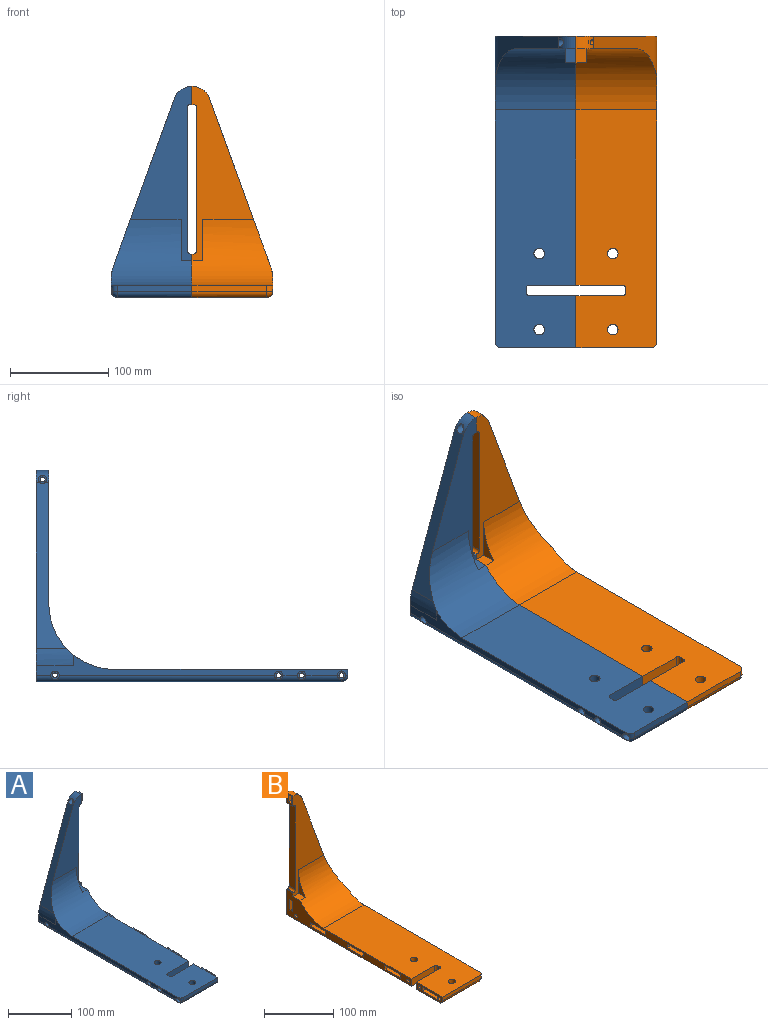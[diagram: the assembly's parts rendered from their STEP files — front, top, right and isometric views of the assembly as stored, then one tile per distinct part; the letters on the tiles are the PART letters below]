
ASSEMBLY  parts=2 mates=1
PART A: 103 faces, bbox 89.6x318.3x216.2 mm
  f0: plane 3.81x1.78mm, normal (1,0,0), area 5.5mm2, adj f79,f80,f81,f82
  f1: cylinder r=19.05mm len=17.9mm, axis (0,1,0), area 230.7mm2, adj f8,f12,f20,f26,f76
  f2: plane 311.15x20.61mm, normal (-1,0,0), area 2200.3mm2, adj f9,f10,f21,f22,f26,f27,f34,f68
  f3: cylinder r=2.54mm len=69.8mm, axis (1,0,0), area 1114mm2, adj f36,f75
  f4: cylinder r=2.54mm len=69.8mm, axis (1,0,0), area 1114mm2, adj f36,f73
  f5: cylinder r=2.54mm len=69.8mm, axis (1,0,0), area 1114mm2, adj f7,f71
  f6: cylinder r=2.54mm len=69.8mm, axis (1,0,0), area 1114mm2, adj f7,f69
  f7: plane 253.49x44.45mm, normal (1,0,0), area 3618.5mm2, adj f5,f6,f9,f10,f11,f12,f14,f18
  f8: plane 18.57x12.7mm, normal (1,0,0), area 155.2mm2, adj f1,f12,f13,f26,f37,f38,f39,f40
  f9: cylinder r=66.9mm len=82.5mm, axis (-1,0,0), area 7217.9mm2, adj f2,f7,f10,f12,f19,f20,f21,f34
  f10: plane 242.57x82.5mm, normal (0,0,1), area 19276.3mm2, adj f2,f7,f9,f15,f17,f18,f27,f29
  f11: plane 311.15x76.15mm, normal (0,0,-1), area 22967mm2, adj f7,f16,f17,f18,f22,f26,f29,f30
  f12: plane 177.32x62.83mm, normal (0,-1,0), area 4884.6mm2, adj f1,f7,f8,f9,f13,f14,f19,f20
  f13: plane 12.7x1.59mm, normal (0,0,-1), area 20.2mm2, adj f8,f12,f25,f26
  f14: plane 12.7x1.59mm, normal (0,0,1), area 20.2mm2, adj f7,f12,f23,f26
  f15: plane 76.15x6.35mm, normal (0,-1,0), area 483.6mm2, adj f10,f16,f27,f36
  f16: cylinder r=6.35mm len=76.15mm, axis (-1,0,0), area 759.6mm2, adj f11,f15,f28,f36
  f17: plane 47.63x12.7mm, normal (0,1,0), area 604.8mm2, adj f10,f11,f30,f36
  f18: plane 47.63x12.7mm, normal (0,-1,0), area 604.8mm2, adj f7,f10,f11,f31
  f19: plane 14.3x11.11mm, normal (0,0,1), area 158.9mm2, adj f7,f9,f12,f35
  f20: plane 169.83x62.3mm, normal (-0.94,0,0.34), area 2553.6mm2, adj f1,f9,f12,f21,f26,f76
  f21: cylinder r=50.8mm len=38.1mm, axis (0,1,0), area 649.1mm2, adj f2,f9,f20,f26,f34
  f22: cylinder r=6.35mm len=311.15mm, axis (0,1,0), area 2999.9mm2, adj f2,f11,f26,f28,f68,f70,f72,f74
  f23: cylinder r=3.18mm len=12.7mm, axis (0,1,0), area 63.3mm2, adj f12,f14,f24,f26
  f24: plane 146.05x12.7mm, normal (1,0,0), area 1854.8mm2, adj f12,f23,f25,f26
  f25: cylinder r=3.17mm len=12.7mm, axis (0,1,0), area 63.3mm2, adj f12,f13,f24,f26
  f26: plane 215.42x82.5mm, normal (0,1,0), area 10433.9mm2, adj f1,f2,f7,f8,f11,f13,f14,f20
  f27: cylinder r=6.35mm len=6.35mm, axis (0,0,1), area 47.8mm2, adj f2,f10,f15,f28,f72
  f28: bspline ~9.47x6.35mm, area 46.7mm2, adj f16,f22,f27,f72
  f29: plane 12.7x4.45mm, normal (1,0,0), area 56.5mm2, adj f10,f11,f30,f31
  f30: cylinder r=3.17mm len=12.7mm, axis (0,0,1), area 63.3mm2, adj f10,f11,f17,f29
  f31: cylinder r=3.17mm len=12.7mm, axis (0,0,1), area 63.3mm2, adj f10,f11,f18,f29
  f32: cylinder r=5.4mm len=12.7mm, axis (0,0,1), area 430.7mm2, adj f10,f11
  f33: cylinder r=5.4mm len=12.7mm, axis (0,0,1), area 430.7mm2, adj f10,f11
  f34: plane 10.52x1.1mm, normal (0,1,0), area 3.8mm2, adj f2,f9,f21
  f35: plane 41.33x14.3mm, normal (1,0,0), area 187.7mm2, adj f9,f12,f19
  f36: plane 53.21x12.7mm, normal (1,0,0), area 425mm2, adj f3,f4,f10,f11,f15,f16,f17,f48
  f37: plane 12.7x5.08mm, normal (0,1,0), area 64.5mm2, adj f8,f38,f40,f80
  f38: plane 6.35x5.08mm, normal (0,0,1), area 32.3mm2, adj f8,f37,f39,f78
  f39: plane 12.7x5.08mm, normal (0,-1,0), area 64.5mm2, adj f8,f38,f40,f81
  f40: plane 6.35x5.08mm, normal (0,0,-1), area 32.3mm2, adj f8,f37,f39,f82
  f41: cylinder r=2.54mm len=14.48mm, axis (-1,0,0), area 231.1mm2, adj f77,f79
  f42: plane 3.81x1.78mm, normal (1,0,0), area 5.5mm2, adj f78,f79,f80,f81
  f43: plane 6.35x5.08mm, normal (0,0,1), area 32.3mm2, adj f7,f44,f46,f84
  f44: plane 19.05x5.08mm, normal (0,-1,0), area 96.8mm2, adj f7,f43,f45,f86
  f45: plane 6.35x5.08mm, normal (0,0,-1), area 32.3mm2, adj f7,f44,f46,f85
  f46: plane 19.05x5.08mm, normal (0,1,0), area 96.8mm2, adj f7,f43,f45,f83
  f47: plane 16.51x3.81mm, normal (1,0,0), area 62.9mm2, adj f83,f84,f85,f86
  f48: plane 31.75x5.08mm, normal (0,0,1), area 161.3mm2, adj f36,f49,f51,f99
  f49: plane 6.35x5.08mm, normal (0,-1,0), area 32.3mm2, adj f36,f48,f50,f100
  f50: plane 31.75x5.08mm, normal (0,0,-1), area 161.3mm2, adj f36,f49,f51,f102
  f51: plane 6.35x5.08mm, normal (0,1,0), area 32.3mm2, adj f36,f48,f50,f101
  f52: plane 29.21x3.81mm, normal (1,0,0), area 111.3mm2, adj f99,f100,f101,f102
  f53: plane 6.35x5.08mm, normal (0,-1,0), area 32.3mm2, adj f7,f54,f56,f96
  f54: plane 31.75x5.08mm, normal (0,0,-1), area 161.3mm2, adj f7,f53,f55,f98
  f55: plane 6.35x5.08mm, normal (0,1,0), area 32.3mm2, adj f7,f54,f56,f97
  f56: plane 31.75x5.08mm, normal (0,0,1), area 161.3mm2, adj f7,f53,f55,f95
  f57: plane 29.21x3.81mm, normal (1,0,0), area 111.3mm2, adj f95,f96,f97,f98
  f58: plane 6.35x5.08mm, normal (0,-1,0), area 32.3mm2, adj f7,f59,f61,f91
  f59: plane 31.75x5.08mm, normal (0,0,-1), area 161.3mm2, adj f7,f58,f60,f93
  f60: plane 6.35x5.08mm, normal (0,1,0), area 32.3mm2, adj f7,f59,f61,f94
  f61: plane 31.75x5.08mm, normal (0,0,1), area 161.3mm2, adj f7,f58,f60,f92
  f62: plane 29.21x3.81mm, normal (1,0,0), area 111.3mm2, adj f91,f92,f93,f94
  f63: plane 6.35x5.08mm, normal (0,-1,0), area 32.3mm2, adj f7,f64,f66,f88
  f64: plane 31.75x5.08mm, normal (0,0,-1), area 161.3mm2, adj f7,f63,f65,f90
  f65: plane 6.35x5.08mm, normal (0,1,0), area 32.3mm2, adj f7,f64,f66,f89
  f66: plane 31.75x5.08mm, normal (0,0,1), area 161.3mm2, adj f7,f63,f65,f87
  f67: plane 29.21x3.81mm, normal (1,0,0), area 111.3mm2, adj f87,f88,f89,f90
  f68: cylinder r=4.31mm len=12.7mm, axis (-1,0,0), area 343.5mm2, adj f2,f22,f69
  f69: plane 8.61x8.61mm, normal (-1,0,0), area 38mm2, adj f6,f68
  f70: cylinder r=4.31mm len=12.7mm, axis (-1,0,0), area 343.5mm2, adj f2,f22,f71
  f71: plane 8.61x8.61mm, normal (-1,0,0), area 38mm2, adj f5,f70
  f72: cylinder r=4.31mm len=12.7mm, axis (-1,0,0), area 320.8mm2, adj f2,f22,f27,f28,f73
  f73: plane 8.61x8.61mm, normal (-1,0,0), area 38mm2, adj f4,f72
  f74: cylinder r=4.31mm len=12.7mm, axis (-1,0,0), area 343.5mm2, adj f2,f22,f75
  f75: plane 8.61x8.61mm, normal (-1,0,0), area 38mm2, adj f3,f74
  f76: cylinder r=4.31mm len=8.61mm, axis (-1,0,0), area 176mm2, adj f1,f20,f77
  f77: plane 8.61x8.61mm, normal (-1,0,0), area 38mm2, adj f41,f76
  f78: cylinder r=1.27mm len=6.35mm, axis (0,1,0), area 10.1mm2, adj f38,f42,f80,f81
  f79: torus R=3.81mm, axis (1,0,0), area 27.4mm2, adj f0,f41,f42,f80,f81
  f80: cylinder r=1.27mm len=12.7mm, axis (0,0,-1), area 18.3mm2, adj f0,f37,f42,f78,f79,f82
  f81: cylinder r=1.27mm len=12.7mm, axis (0,0,1), area 18.3mm2, adj f0,f39,f42,f78,f79,f82
  f82: cylinder r=1.27mm len=6.35mm, axis (0,-1,0), area 10.1mm2, adj f0,f40,f80,f81
  f83: cylinder r=1.27mm len=19.05mm, axis (0,0,-1), area 35.5mm2, adj f46,f47,f84,f85
  f84: cylinder r=1.27mm len=6.35mm, axis (0,1,0), area 10.1mm2, adj f43,f47,f83,f86
  f85: cylinder r=1.27mm len=6.35mm, axis (0,-1,0), area 10.1mm2, adj f45,f47,f83,f86
  f86: cylinder r=1.27mm len=19.05mm, axis (0,0,1), area 35.5mm2, adj f44,f47,f84,f85
  f87: cylinder r=1.27mm len=31.75mm, axis (0,1,0), area 60.8mm2, adj f66,f67,f88,f89
  f88: cylinder r=1.27mm len=6.35mm, axis (0,0,1), area 10.1mm2, adj f63,f67,f87,f90
  f89: cylinder r=1.27mm len=6.35mm, axis (0,0,-1), area 10.1mm2, adj f65,f67,f87,f90
  f90: cylinder r=1.27mm len=31.75mm, axis (0,-1,0), area 60.8mm2, adj f64,f67,f88,f89
  f91: cylinder r=1.27mm len=6.35mm, axis (0,0,1), area 10.1mm2, adj f58,f62,f92,f93
  f92: cylinder r=1.27mm len=31.75mm, axis (0,1,0), area 60.8mm2, adj f61,f62,f91,f94
  f93: cylinder r=1.27mm len=31.75mm, axis (0,-1,0), area 60.8mm2, adj f59,f62,f91,f94
  f94: cylinder r=1.27mm len=6.35mm, axis (0,0,-1), area 10.1mm2, adj f60,f62,f92,f93
  f95: cylinder r=1.27mm len=31.75mm, axis (0,1,0), area 60.8mm2, adj f56,f57,f96,f97
  f96: cylinder r=1.27mm len=6.35mm, axis (0,0,1), area 10.1mm2, adj f53,f57,f95,f98
  f97: cylinder r=1.27mm len=6.35mm, axis (0,0,-1), area 10.1mm2, adj f55,f57,f95,f98
  f98: cylinder r=1.27mm len=31.75mm, axis (0,-1,0), area 60.8mm2, adj f54,f57,f96,f97
  f99: cylinder r=1.27mm len=31.75mm, axis (0,1,0), area 60.8mm2, adj f48,f52,f100,f101
  f100: cylinder r=1.27mm len=6.35mm, axis (0,0,1), area 10.1mm2, adj f49,f52,f99,f102
  f101: cylinder r=1.27mm len=6.35mm, axis (0,0,-1), area 10.1mm2, adj f51,f52,f99,f102
  f102: cylinder r=1.27mm len=31.75mm, axis (0,-1,0), area 60.8mm2, adj f50,f52,f100,f101
PART B: 116 faces, bbox 82.6x317.5x215.4 mm
  f0: cylinder r=2.54mm len=5.08mm, axis (-1,0,0), area 56.2mm2, adj f8,f110
  f1: cylinder r=2.54mm len=62.23mm, axis (-1,0,0), area 993.1mm2, adj f6,f107
  f2: cylinder r=2.54mm len=62.23mm, axis (-1,0,0), area 993.1mm2, adj f6,f99
  f3: cylinder r=2.54mm len=62.23mm, axis (-1,0,0), area 993.1mm2, adj f5,f91
  f4: cylinder r=2.54mm len=62.23mm, axis (-1,0,0), area 993.1mm2, adj f5,f83
  f5: plane 253.49x44.45mm, normal (-1,0,0), area 3653.7mm2, adj f3,f4,f12,f14,f15,f16,f23,f25
  f6: plane 53.21x12.7mm, normal (-1,0,0), area 434.6mm2, adj f1,f2,f14,f15,f26,f27,f28,f51
  f7: plane 18.57x12.7mm, normal (-1,0,0), area 159.9mm2, adj f8,f16,f19,f25,f46,f47,f48,f49
  f8: cylinder r=19.05mm len=17.9mm, axis (0,1,0), area 271.7mm2, adj f0,f7,f16,f17,f25,f108,f109,f110
  f9: cylinder r=6.35mm len=311.15mm, axis (0,1,0), area 3069.2mm2, adj f10,f15,f18,f25,f42,f43,f44,f45
  f10: bspline ~9.47x6.35mm, area 59.7mm2, adj f9,f11,f27,f43
  f11: cylinder r=6.35mm len=6.35mm, axis (0,0,-1), area 60mm2, adj f10,f14,f18,f26,f43
  f12: cylinder r=66.9mm len=82.6mm, axis (-1,0,0), area 7223.1mm2, adj f5,f13,f14,f16,f17,f24,f36,f37
  f13: plane 36.83x14.26mm, normal (1,0,0), area 183.8mm2, adj f12,f36,f37
  f14: plane 242.57x82.5mm, normal (0,0,1), area 19276.3mm2, adj f5,f6,f11,f12,f18,f26,f28,f29
  f15: plane 311.15x76.15mm, normal (0,0,-1), area 22967mm2, adj f5,f6,f9,f25,f27,f28,f29,f30
  f16: plane 177.32x62.83mm, normal (0,-1,0), area 4884.6mm2, adj f5,f7,f8,f12,f17,f19,f20,f21
  f17: plane 169.07x61.54mm, normal (0.94,0,0.34), area 2558mm2, adj f8,f12,f16,f24,f25
  f18: plane 311.15x10.09mm, normal (1,0,0), area 1987.9mm2, adj f9,f11,f14,f24,f25,f35,f36,f42
  f19: plane 12.7x1.59mm, normal (0,0,-1), area 20.2mm2, adj f7,f16,f20,f25
  f20: cylinder r=3.18mm len=12.7mm, axis (0,1,0), area 63.3mm2, adj f16,f19,f21,f25
  f21: plane 146.05x12.7mm, normal (-1,0,0), area 1854.8mm2, adj f16,f20,f22,f25
  f22: cylinder r=3.17mm len=12.7mm, axis (0,1,0), area 63.3mm2, adj f16,f21,f23,f25
  f23: plane 12.7x1.59mm, normal (0,0,1), area 20.2mm2, adj f5,f16,f22,f25
  f24: cylinder r=50.8mm len=38.1mm, axis (0,1,0), area 649.1mm2, adj f12,f17,f18,f25,f37,f38
  f25: plane 215.42x82.5mm, normal (0,1,0), area 10433.9mm2, adj f5,f7,f8,f9,f15,f17,f18,f19
  f26: plane 76.15x6.35mm, normal (0,-1,0), area 483.6mm2, adj f6,f11,f14,f27
  f27: cylinder r=6.35mm len=76.15mm, axis (-1,0,0), area 759.6mm2, adj f6,f10,f15,f26
  f28: plane 47.63x12.7mm, normal (0,1,0), area 604.8mm2, adj f6,f14,f15,f29
  f29: cylinder r=3.17mm len=12.7mm, axis (0,0,1), area 63.3mm2, adj f14,f15,f28,f30
  f30: plane 12.7x4.45mm, normal (-1,0,0), area 56.5mm2, adj f14,f15,f29,f31
  f31: cylinder r=3.17mm len=12.7mm, axis (0,0,1), area 63.3mm2, adj f14,f15,f30,f32
  f32: plane 47.63x12.7mm, normal (0,-1,0), area 604.8mm2, adj f5,f14,f15,f31
  f33: cylinder r=5.4mm len=12.7mm, axis (0,0,1), area 430.7mm2, adj f14,f15
  f34: cylinder r=5.4mm len=12.7mm, axis (0,0,1), area 430.7mm2, adj f14,f15
  f35: plane 3.74x0.1mm, normal (0,1,0), area 0.2mm2, adj f18,f36,f38
  f36: plane 62.23x0.1mm, normal (0,0,-1), area 6.2mm2, adj f12,f13,f18,f35,f38
  f37: plane 14.26x1.2mm, normal (0,1,0), area 5.1mm2, adj f12,f13,f24,f38
  f38: plane 25.4x3.74mm, normal (1,0,0.03), area 95.1mm2, adj f24,f35,f36,f37
  f39: plane 14.3x11.11mm, normal (0,0,1), area 158.9mm2, adj f5,f12,f16,f40
  f40: plane 41.33x14.3mm, normal (-1,0,0), area 187.7mm2, adj f12,f16,f39
  f41: cylinder r=2.54mm len=5.08mm, axis (-1,0,0), area 25.9mm2, adj f50,f115
  f42: cylinder r=2.54mm len=16.16mm, axis (-1,0,0), area 257.8mm2, adj f9,f18,f106
  f43: cylinder r=2.54mm len=16.16mm, axis (-1,0,0), area 253.6mm2, adj f9,f10,f11,f18,f98
  f44: cylinder r=2.54mm len=16.16mm, axis (-1,0,0), area 257.8mm2, adj f9,f18,f90
  f45: cylinder r=2.54mm len=16.16mm, axis (-1,0,0), area 257.8mm2, adj f9,f18,f82
  f46: plane 6.99x6.1mm, normal (0,0,1), area 42.6mm2, adj f7,f47,f49,f50
  f47: plane 12.45x6.99mm, normal (0,-1,0), area 86.9mm2, adj f7,f46,f48,f50
  f48: plane 6.99x6.1mm, normal (0,0,-1), area 42.6mm2, adj f7,f47,f49,f50
  f49: plane 12.45x6.99mm, normal (0,1,0), area 86.9mm2, adj f7,f46,f48,f50
  f50: plane 12.45x6.1mm, normal (-1,0,0), area 55.6mm2, adj f41,f46,f47,f48,f49
  f51: plane 6.99x6.1mm, normal (0,-1,0), area 42.6mm2, adj f6,f52,f54,f55
  f52: plane 31.5x6.99mm, normal (0,0,-1), area 220mm2, adj f6,f51,f53,f55
  f53: plane 6.99x6.1mm, normal (0,1,0), area 42.6mm2, adj f6,f52,f54,f55
  f54: plane 31.5x6.99mm, normal (0,0,1), area 220mm2, adj f6,f51,f53,f55
  f55: plane 31.5x6.1mm, normal (-1,0,0), area 192mm2, adj f51,f52,f53,f54
  f56: plane 31.5x6.99mm, normal (0,0,-1), area 220mm2, adj f5,f57,f59,f60
  f57: plane 6.99x6.1mm, normal (0,1,0), area 42.6mm2, adj f5,f56,f58,f60
  f58: plane 31.5x6.99mm, normal (0,0,1), area 220mm2, adj f5,f57,f59,f60
  f59: plane 6.99x6.1mm, normal (0,-1,0), area 42.6mm2, adj f5,f56,f58,f60
  f60: plane 31.5x6.1mm, normal (-1,0,0), area 192mm2, adj f56,f57,f58,f59
  f61: plane 31.5x6.99mm, normal (0,0,-1), area 220mm2, adj f5,f62,f64,f65
  f62: plane 6.99x6.1mm, normal (0,1,0), area 42.6mm2, adj f5,f61,f63,f65
  f63: plane 31.5x6.99mm, normal (0,0,1), area 220mm2, adj f5,f62,f64,f65
  f64: plane 6.99x6.1mm, normal (0,-1,0), area 42.6mm2, adj f5,f61,f63,f65
  f65: plane 31.5x6.1mm, normal (-1,0,0), area 192mm2, adj f61,f62,f63,f64
  f66: plane 31.5x6.99mm, normal (0,0,-1), area 220mm2, adj f5,f67,f69,f70
  f67: plane 6.99x6.1mm, normal (0,1,0), area 42.6mm2, adj f5,f66,f68,f70
  f68: plane 31.5x6.99mm, normal (0,0,1), area 220mm2, adj f5,f67,f69,f70
  f69: plane 6.99x6.1mm, normal (0,-1,0), area 42.6mm2, adj f5,f66,f68,f70
  f70: plane 31.5x6.1mm, normal (-1,0,0), area 192mm2, adj f66,f67,f68,f69
  f71: plane 18.8x6.99mm, normal (0,-1,0), area 131.3mm2, adj f5,f72,f74,f75
  f72: plane 6.99x6.1mm, normal (0,0,-1), area 42.6mm2, adj f5,f71,f73,f75
  f73: plane 18.8x6.99mm, normal (0,1,0), area 131.3mm2, adj f5,f72,f74,f75
  f74: plane 6.99x6.1mm, normal (0,0,1), area 42.6mm2, adj f5,f71,f73,f75
  f75: plane 18.8x6.1mm, normal (-1,0,0), area 114.6mm2, adj f71,f72,f73,f74
  f76: plane 4.68x4.12mm, normal (0,-1,0), area 19.2mm2, adj f77,f81,f82,f83
  f77: plane 4.12x4.05mm, normal (0,-0.5,-0.87), area 19.2mm2, adj f76,f78,f82,f83
  f78: plane 4.12x4.05mm, normal (0,0.5,-0.87), area 19.2mm2, adj f77,f79,f82,f83
  f79: plane 4.68x4.12mm, normal (0,1,0), area 19.2mm2, adj f78,f80,f82,f83
  f80: plane 4.12x4.05mm, normal (0,0.5,0.87), area 19.2mm2, adj f79,f81,f82,f83
  f81: plane 4.12x4.05mm, normal (0,-0.5,0.87), area 19.2mm2, adj f76,f80,f82,f83
  f82: plane 9.36x8.1mm, normal (-1,0,0), area 36.6mm2, adj f45,f76,f77,f78,f79,f80,f81
  f83: plane 9.36x8.1mm, normal (1,0,0), area 36.6mm2, adj f4,f76,f77,f78,f79,f80,f81
  f84: plane 4.68x4.12mm, normal (0,-1,0), area 19.2mm2, adj f85,f89,f90,f91
  f85: plane 4.12x4.05mm, normal (0,-0.5,-0.87), area 19.2mm2, adj f84,f86,f90,f91
  f86: plane 4.12x4.05mm, normal (0,0.5,-0.87), area 19.2mm2, adj f85,f87,f90,f91
  f87: plane 4.68x4.12mm, normal (0,1,0), area 19.2mm2, adj f86,f88,f90,f91
  f88: plane 4.12x4.05mm, normal (0,0.5,0.87), area 19.2mm2, adj f87,f89,f90,f91
  f89: plane 4.12x4.05mm, normal (0,-0.5,0.87), area 19.2mm2, adj f84,f88,f90,f91
  f90: plane 9.36x8.1mm, normal (-1,0,0), area 36.6mm2, adj f44,f84,f85,f86,f87,f88,f89
  f91: plane 9.36x8.1mm, normal (1,0,0), area 36.6mm2, adj f3,f84,f85,f86,f87,f88,f89
  f92: plane 4.68x4.12mm, normal (0,-1,0), area 19.2mm2, adj f93,f97,f98,f99
  f93: plane 4.12x4.05mm, normal (0,-0.5,-0.87), area 19.2mm2, adj f92,f94,f98,f99
  f94: plane 4.12x4.05mm, normal (0,0.5,-0.87), area 19.2mm2, adj f93,f95,f98,f99
  f95: plane 4.68x4.12mm, normal (0,1,0), area 19.2mm2, adj f94,f96,f98,f99
  f96: plane 4.12x4.05mm, normal (0,0.5,0.87), area 19.2mm2, adj f95,f97,f98,f99
  f97: plane 4.12x4.05mm, normal (0,-0.5,0.87), area 19.2mm2, adj f92,f96,f98,f99
  f98: plane 9.36x8.1mm, normal (-1,0,0), area 36.6mm2, adj f43,f92,f93,f94,f95,f96,f97
  f99: plane 9.36x8.1mm, normal (1,0,0), area 36.6mm2, adj f2,f92,f93,f94,f95,f96,f97
  f100: plane 4.68x4.12mm, normal (0,-1,0), area 19.2mm2, adj f101,f105,f106,f107
  f101: plane 4.12x4.05mm, normal (0,-0.5,-0.87), area 19.2mm2, adj f100,f102,f106,f107
  f102: plane 4.12x4.05mm, normal (0,0.5,-0.87), area 19.2mm2, adj f101,f103,f106,f107
  f103: plane 4.68x4.12mm, normal (0,1,0), area 19.2mm2, adj f102,f104,f106,f107
  f104: plane 4.12x4.05mm, normal (0,0.5,0.87), area 19.2mm2, adj f103,f105,f106,f107
  f105: plane 4.12x4.05mm, normal (0,-0.5,0.87), area 19.2mm2, adj f100,f104,f106,f107
  f106: plane 9.36x8.1mm, normal (-1,0,0), area 36.6mm2, adj f42,f100,f101,f102,f103,f104,f105
  f107: plane 9.36x8.1mm, normal (1,0,0), area 36.6mm2, adj f1,f100,f101,f102,f103,f104,f105
  f108: plane 4.09x4.05mm, normal (0,0.5,-0.87), area 19.1mm2, adj f8,f109,f110,f111,f115
  f109: plane 4.09x4.05mm, normal (0,-0.5,-0.87), area 19.1mm2, adj f8,f108,f110,f112,f115
  f110: plane 9.11x8.1mm, normal (-1,0,0), area 36.5mm2, adj f0,f8,f108,f109,f111,f112,f113,f114
  f111: plane 4.68x4.09mm, normal (0,1,0), area 19.1mm2, adj f108,f110,f114,f115
  f112: plane 4.68x4.09mm, normal (0,-1,0), area 19.1mm2, adj f109,f110,f113,f115
  f113: plane 4.09x4.05mm, normal (0,-0.5,0.87), area 19.1mm2, adj f110,f112,f114,f115
  f114: plane 4.09x4.05mm, normal (0,0.5,0.87), area 19.1mm2, adj f110,f111,f113,f115
  f115: plane 9.36x8.1mm, normal (1,0,0), area 36.6mm2, adj f41,f108,f109,f111,f112,f113,f114
PLACE A t=(-153.24,66.54,-41.37)mm
PLACE B t=(-153.24,66.54,-41.37)mm
MATE fastened A.f6 <-> B.f3  axis (1,0,0) through (-153.24,-180.6,-142.72)mm
